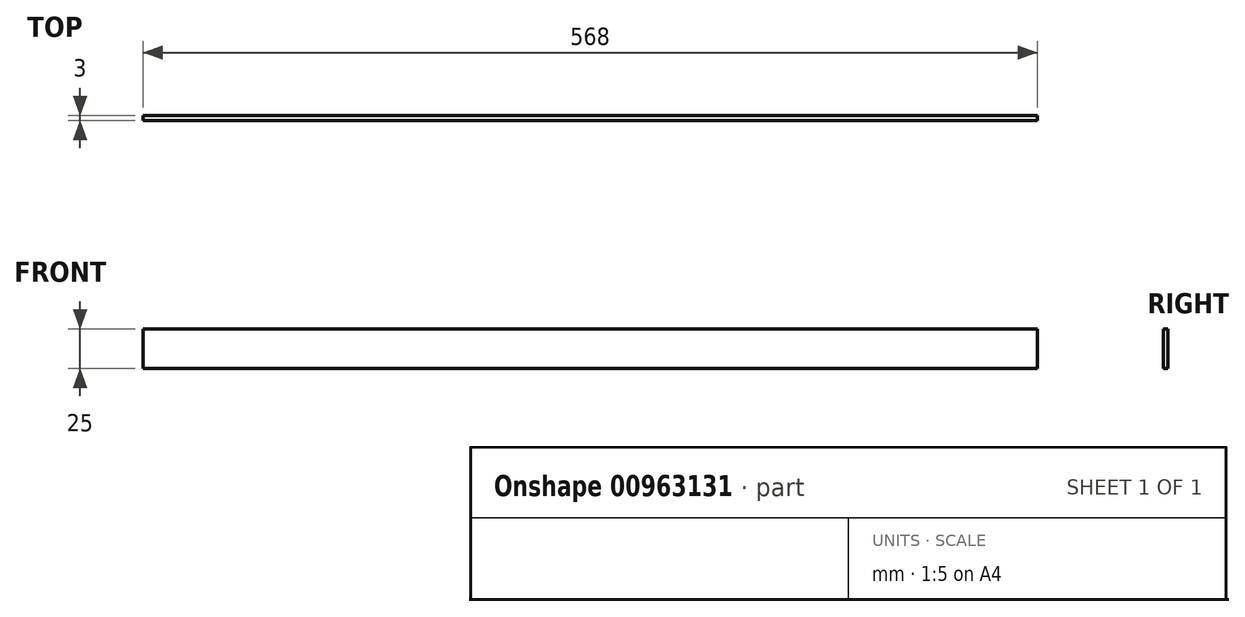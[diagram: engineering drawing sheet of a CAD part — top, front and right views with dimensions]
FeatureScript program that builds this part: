
annotation { "Feature Type Name" : "Feature", "Feature Type Description" : "" }
export const myFeature = defineFeature(function(context is Context, id is Id, definition is map)
    precondition{}
    {
        {
            var Q0;
            Q0=qCreatedBy(makeId("Front.planeOp"),FACE);
            var sketch = newSketch(context, id + "F0", { "sketchPlane" : qUnion([Q0])});
            skLineSegment(sketch, "E0", {"start": v(0, 0) * mm, "end": v(0, -25) * mm});
            skLineSegment(sketch, "E1", {"start": v(0, -25) * mm, "end": v(568, -25) * mm});
            skPoint(sketch, "E2.endSnap0", {"position": v(0, -12.5) * mm});
            skLineSegment(sketch, "E3", {"start": v(568, -25) * mm, "end": v(568, 0) * mm});
            skLineSegment(sketch, "E4", {"start": v(568, 0) * mm, "end": v(0, 0) * mm});
            skSolve(sketch);
        }
        {
            var Q0;
            Q0=makeQuery(id+"F0.imprint","IMPRINT",FACE,{"disambiguationData":[TD([[makeQuery(id+"F0.imprint","IMPRINT",EDGE,{"derivedFrom":sQuery(id+"F0.wireOp",EDGE,"E0")}),1.0]])]});
            extrude(context, id + "F1", {"entities" : qUnion([Q0]), "depth" : 3 * mm, "offsetDistance" : 25 * mm});
        }
    });
